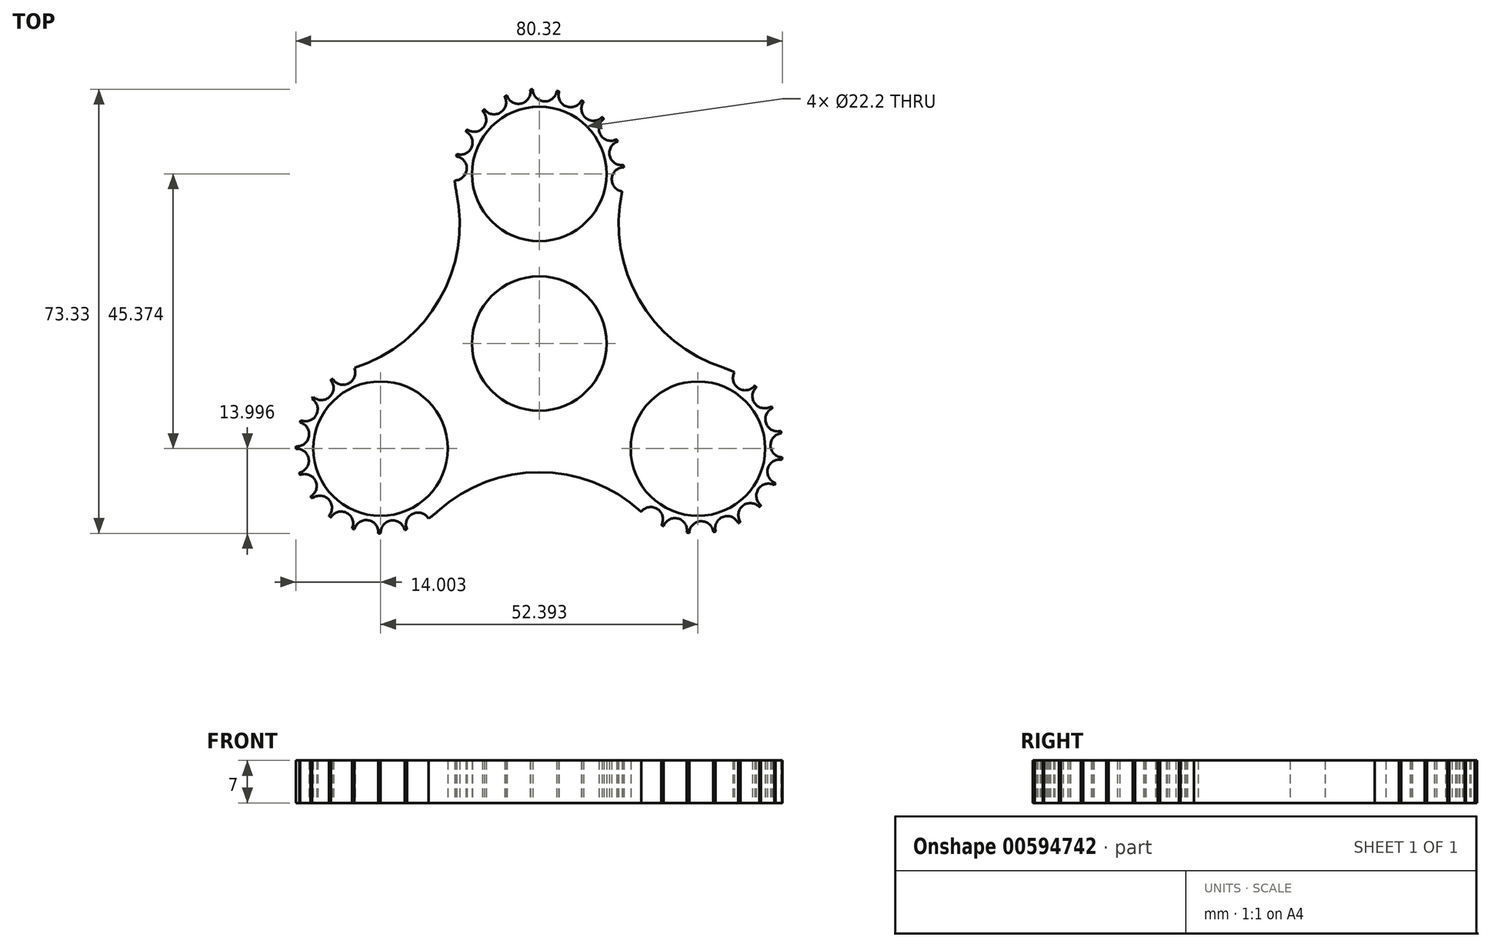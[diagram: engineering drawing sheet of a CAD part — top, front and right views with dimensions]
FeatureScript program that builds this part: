
annotation { "Feature Type Name" : "Feature", "Feature Type Description" : "" }
export const myFeature = defineFeature(function(context is Context, id is Id, definition is map)
    precondition{}
    {
        {
            var Q0;
            Q0=qCreatedBy(makeId("Top.planeOp"),FACE);
            var sketch = newSketch(context, id + "F0", { "sketchPlane" : qUnion([Q0])});
            skCircle(sketch, "E0", {"center": v(0, 0) * mm, "radius": 11.1 * mm});
            skArc(sketch, "E1", {"start": v(13.96, 29.08) * mm, "mid": v(13.94, 29.28) * mm, "end": v(13.92, 29.48) * mm});
            skArc(sketch, "E2.1.0", {"start": v(-34.11, -5.83) * mm, "mid": v(-34.28, -5.94) * mm, "end": v(-34.44, -6.06) * mm});
            skArc(sketch, "E2.2.0", {"start": v(16.8, -27.75) * mm, "mid": v(16.82, -27.77) * mm, "end": v(16.84, -27.79) * mm});
            skPoint(sketch, "E2.center", {"position": v(0, -2.25) * mm});
            skArc(sketch, "E3", {"start": v(-30.48, -4.04) * mm, "mid": v(-16.47, 7.26) * mm, "end": v(-13.68, 25.04) * mm});
            skArc(sketch, "E4", {"start": v(16.8, -27.75) * mm, "mid": v(0, -21.27) * mm, "end": v(-16.8, -27.75) * mm});
            skArc(sketch, "E5", {"start": v(13.68, 25.04) * mm, "mid": v(16.47, 7.26) * mm, "end": v(30.48, -4.04) * mm});
            skCircle(sketch, "E6", {"center": v(26.2, -17.37) * mm, "radius": 11.1 * mm});
            skCircle(sketch, "E7", {"center": v(0, 28) * mm, "radius": 11.1 * mm});
            skCircle(sketch, "E8", {"center": v(-26.2, -17.37) * mm, "radius": 11.1 * mm});
            skArc(sketch, "E9", {"start": v(-1.08, 41.96) * mm, "mid": v(0.79, 39.97) * mm, "end": v(2.9, 41.7) * mm});
            skArc(sketch, "E10.1.0", {"start": v(-5.34, 40.94) * mm, "mid": v(-2.95, 39.63) * mm, "end": v(-1.48, 41.92) * mm});
            skArc(sketch, "E10.2.0", {"start": v(-9.08, 38.66) * mm, "mid": v(-6.4, 38.15) * mm, "end": v(-5.7, 40.78) * mm});
            skArc(sketch, "E10.3.0", {"start": v(-11.93, 35.33) * mm, "mid": v(-9.23, 35.67) * mm, "end": v(-9.38, 38.4) * mm});
            skArc(sketch, "E10.4.0", {"start": v(-13.6, 31.28) * mm, "mid": v(-11.15, 32.45) * mm, "end": v(-12.13, 34.99) * mm});
            skArc(sketch, "E10.5.0", {"start": v(-13.96, 26.92) * mm, "mid": v(-11.97, 28.79) * mm, "end": v(-13.7, 30.9) * mm});
            skArc(sketch, "E10.15.0", {"start": v(13.96, 29.08) * mm, "mid": v(11.97, 27.21) * mm, "end": v(13.7, 25.1) * mm});
            skArc(sketch, "E10.16.0", {"start": v(12.94, 33.34) * mm, "mid": v(11.63, 30.95) * mm, "end": v(13.92, 29.48) * mm});
            skArc(sketch, "E10.17.0", {"start": v(10.66, 37.08) * mm, "mid": v(10.15, 34.4) * mm, "end": v(12.78, 33.7) * mm});
            skArc(sketch, "E10.18.0", {"start": v(7.33, 39.93) * mm, "mid": v(7.67, 37.23) * mm, "end": v(10.4, 37.38) * mm});
            skArc(sketch, "E10.19.0", {"start": v(3.28, 41.6) * mm, "mid": v(4.45, 39.15) * mm, "end": v(6.99, 40.13) * mm});
            skArc(sketch, "E11.trimOffspring", {"start": v(13.62, 24.72) * mm, "mid": v(13.61, 24.72) * mm, "end": v(13.6, 24.72) * mm});
            skArc(sketch, "E12.trimOffspring", {"start": v(12.94, 33.34) * mm, "mid": v(12.86, 33.53) * mm, "end": v(12.78, 33.7) * mm});
            skArc(sketch, "E13.trimOffspring", {"start": v(10.66, 37.08) * mm, "mid": v(10.53, 37.23) * mm, "end": v(10.4, 37.38) * mm});
            skArc(sketch, "E14.trimOffspring", {"start": v(7.33, 39.93) * mm, "mid": v(7.16, 40.03) * mm, "end": v(6.99, 40.13) * mm});
            skArc(sketch, "E15.trimOffspring", {"start": v(3.28, 41.6) * mm, "mid": v(3.1, 41.65) * mm, "end": v(2.9, 41.7) * mm});
            skArc(sketch, "E16.trimOffspring", {"start": v(-1.08, 41.96) * mm, "mid": v(-1.28, 41.94) * mm, "end": v(-1.48, 41.92) * mm});
            skArc(sketch, "E17.trimOffspring", {"start": v(-5.34, 40.94) * mm, "mid": v(-5.53, 40.86) * mm, "end": v(-5.7, 40.78) * mm});
            skArc(sketch, "E18.trimOffspring", {"start": v(-9.08, 38.66) * mm, "mid": v(-9.23, 38.53) * mm, "end": v(-9.38, 38.4) * mm});
            skArc(sketch, "E19.trimOffspring", {"start": v(-11.93, 35.33) * mm, "mid": v(-12.03, 35.16) * mm, "end": v(-12.13, 34.99) * mm});
            skArc(sketch, "E20.trimOffspring", {"start": v(-13.6, 31.28) * mm, "mid": v(-13.65, 31.1) * mm, "end": v(-13.7, 30.9) * mm});
            skArc(sketch, "E21.trimOffspring", {"start": v(-13.96, 26.92) * mm, "mid": v(-13.85, 25.97) * mm, "end": v(-13.68, 25.04) * mm});
            skArc(sketch, "E22.1.0", {"start": v(-18.28, -28.92) * mm, "mid": v(-20.89, -28.14) * mm, "end": v(-21.86, -30.68) * mm});
            skArc(sketch, "E22.1.1", {"start": v(-22.23, -30.8) * mm, "mid": v(-24.48, -29.25) * mm, "end": v(-26.18, -31.37) * mm});
            skArc(sketch, "E22.1.2", {"start": v(-26.58, -31.37) * mm, "mid": v(-28.23, -29.2) * mm, "end": v(-30.5, -30.7) * mm});
            skArc(sketch, "E22.1.3", {"start": v(-30.88, -30.57) * mm, "mid": v(-31.78, -28) * mm, "end": v(-34.41, -28.7) * mm});
            skArc(sketch, "E22.1.4", {"start": v(-34.73, -28.47) * mm, "mid": v(-34.8, -25.75) * mm, "end": v(-37.51, -25.61) * mm});
            skArc(sketch, "E22.1.5", {"start": v(-37.74, -25.3) * mm, "mid": v(-36.96, -22.68) * mm, "end": v(-39.5, -21.71) * mm});
            skArc(sketch, "E22.1.6", {"start": v(-39.62, -21.34) * mm, "mid": v(-38.07, -19.1) * mm, "end": v(-40.2, -17.39) * mm});
            skArc(sketch, "E22.1.7", {"start": v(-40.2, -17) * mm, "mid": v(-38.02, -15.34) * mm, "end": v(-39.52, -13.06) * mm});
            skArc(sketch, "E22.1.8", {"start": v(-39.39, -12.69) * mm, "mid": v(-36.82, -11.79) * mm, "end": v(-37.53, -9.16) * mm});
            skArc(sketch, "E22.1.9", {"start": v(-37.3, -8.84) * mm, "mid": v(-34.57, -8.78) * mm, "end": v(-34.44, -6.06) * mm});
            skArc(sketch, "E22.1.10", {"start": v(-34.11, -5.83) * mm, "mid": v(-31.5, -6.61) * mm, "end": v(-30.54, -4.06) * mm});
            skArc(sketch, "E22.2.0", {"start": v(32.24, -4.74) * mm, "mid": v(32.86, -7.4) * mm, "end": v(35.55, -6.96) * mm});
            skArc(sketch, "E22.2.1", {"start": v(35.84, -7.23) * mm, "mid": v(35.62, -9.95) * mm, "end": v(38.31, -10.36) * mm});
            skArc(sketch, "E22.2.2", {"start": v(38.5, -10.7) * mm, "mid": v(37.46, -13.22) * mm, "end": v(39.89, -14.45) * mm});
            skArc(sketch, "E22.2.3", {"start": v(39.96, -14.84) * mm, "mid": v(38.19, -16.9) * mm, "end": v(40.12, -18.82) * mm});
            skArc(sketch, "E22.2.4", {"start": v(40.07, -19.22) * mm, "mid": v(37.75, -20.63) * mm, "end": v(39, -23.06) * mm});
            skArc(sketch, "E22.2.5", {"start": v(38.83, -23.41) * mm, "mid": v(36.17, -24.04) * mm, "end": v(36.6, -26.73) * mm});
            skArc(sketch, "E22.2.6", {"start": v(36.34, -27.02) * mm, "mid": v(33.63, -26.8) * mm, "end": v(33.2, -29.5) * mm});
            skArc(sketch, "E22.2.7", {"start": v(32.86, -29.68) * mm, "mid": v(30.35, -28.63) * mm, "end": v(29.12, -31.07) * mm});
            skArc(sketch, "E22.2.8", {"start": v(28.73, -31.14) * mm, "mid": v(26.67, -29.36) * mm, "end": v(24.75, -31.3) * mm});
            skArc(sketch, "E22.2.9", {"start": v(24.35, -31.25) * mm, "mid": v(22.94, -28.92) * mm, "end": v(20.51, -30.17) * mm});
            skArc(sketch, "E22.2.10", {"start": v(20.16, -30) * mm, "mid": v(19.53, -27.35) * mm, "end": v(16.84, -27.79) * mm});
            skArc(sketch, "E23.trimOffspring", {"start": v(-39.39, -12.69) * mm, "mid": v(-39.45, -12.87) * mm, "end": v(-39.52, -13.06) * mm});
            skArc(sketch, "E24.trimOffspring", {"start": v(-40.2, -17) * mm, "mid": v(-40.2, -17.2) * mm, "end": v(-40.2, -17.39) * mm});
            skArc(sketch, "E25.trimOffspring", {"start": v(-18.28, -28.92) * mm, "mid": v(-17.52, -28.36) * mm, "end": v(-16.8, -27.75) * mm});
            skArc(sketch, "E26.trimOffspring", {"start": v(-22.23, -30.8) * mm, "mid": v(-22.05, -30.74) * mm, "end": v(-21.86, -30.68) * mm});
            skArc(sketch, "E27.trimOffspring", {"start": v(-30.48, -4.04) * mm, "mid": v(-30.5, -4.05) * mm, "end": v(-30.54, -4.06) * mm});
            skArc(sketch, "E28.trimOffspring", {"start": v(13.6, 24.72) * mm, "mid": v(13.65, 24.9) * mm, "end": v(13.7, 25.1) * mm});
            skArc(sketch, "E29.trimOffspring", {"start": v(-30.88, -30.57) * mm, "mid": v(-30.7, -30.63) * mm, "end": v(-30.5, -30.7) * mm});
            skArc(sketch, "E30.trimOffspring", {"start": v(-34.73, -28.47) * mm, "mid": v(-34.57, -28.6) * mm, "end": v(-34.41, -28.7) * mm});
            skArc(sketch, "E31.trimOffspring", {"start": v(-37.74, -25.3) * mm, "mid": v(-37.63, -25.45) * mm, "end": v(-37.51, -25.61) * mm});
            skArc(sketch, "E32.trimOffspring", {"start": v(-39.62, -21.34) * mm, "mid": v(-39.57, -21.53) * mm, "end": v(-39.5, -21.71) * mm});
            skLineSegment(sketch, "E33", {"start": v(-37.53, -9.16) * mm, "end": v(-37.3, -8.84) * mm});
            skArc(sketch, "E34.trimOffspring", {"start": v(20.16, -30) * mm, "mid": v(20.34, -30.09) * mm, "end": v(20.51, -30.17) * mm});
            skArc(sketch, "E35.trimOffspring", {"start": v(28.73, -31.14) * mm, "mid": v(28.93, -31.1) * mm, "end": v(29.12, -31.07) * mm});
            skLineSegment(sketch, "E36", {"start": v(24.35, -31.25) * mm, "end": v(24.75, -31.3) * mm});
            skLineSegment(sketch, "E37", {"start": v(-26.58, -31.37) * mm, "end": v(-26.18, -31.37) * mm});
            skArc(sketch, "E38.trimOffspring", {"start": v(32.24, -4.74) * mm, "mid": v(31.37, -4.36) * mm, "end": v(30.48, -4.04) * mm});
            skArc(sketch, "E39.trimOffspring", {"start": v(35.84, -7.23) * mm, "mid": v(35.7, -7.1) * mm, "end": v(35.55, -6.96) * mm});
            skArc(sketch, "E40.trimOffspring", {"start": v(38.5, -10.7) * mm, "mid": v(38.41, -10.53) * mm, "end": v(38.31, -10.36) * mm});
            skArc(sketch, "E41.trimOffspring", {"start": v(39.96, -14.84) * mm, "mid": v(39.93, -14.64) * mm, "end": v(39.89, -14.45) * mm});
            skArc(sketch, "E42.trimOffspring", {"start": v(40.07, -19.22) * mm, "mid": v(40.1, -19.02) * mm, "end": v(40.12, -18.82) * mm});
            skArc(sketch, "E43.trimOffspring", {"start": v(36.34, -27.02) * mm, "mid": v(36.48, -26.88) * mm, "end": v(36.6, -26.73) * mm});
            skArc(sketch, "E44.trimOffspring", {"start": v(32.86, -29.68) * mm, "mid": v(33.04, -29.59) * mm, "end": v(33.2, -29.5) * mm});
            skLineSegment(sketch, "E45", {"start": v(38.83, -23.41) * mm, "end": v(39, -23.06) * mm});
            skLineSegment(sketch, "E46", {"start": v(39.56, -19.18) * mm, "end": v(39.56, -18.72) * mm});
            skSolve(sketch);
        }
        {
            var Q0;
            Q0 = qSketchRegion(id + "F0", true);
            extrude(context, id + "F1", {"entities" : qUnion([Q0]), "depth" : 7 * mm, "offsetDistance" : 25 * mm});
        }
    });
